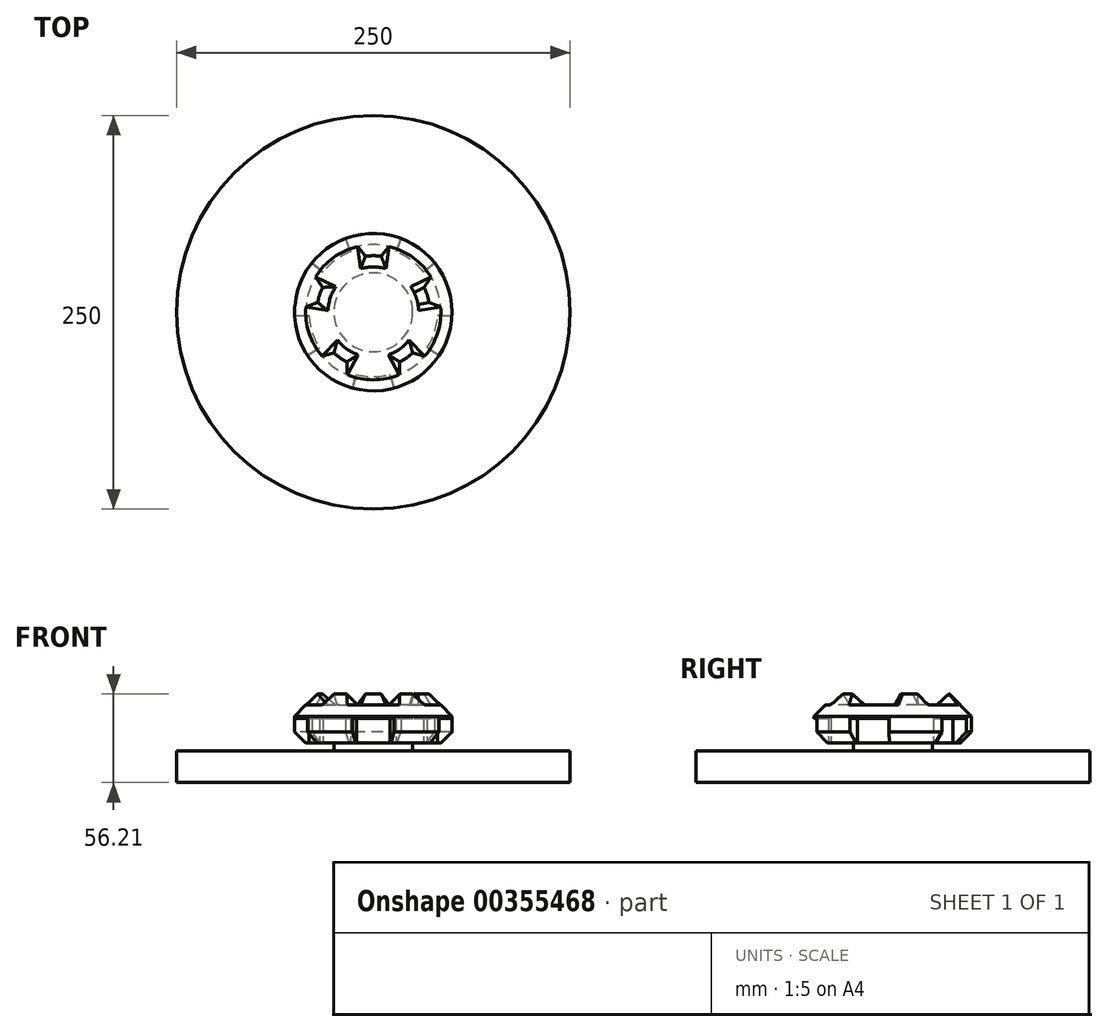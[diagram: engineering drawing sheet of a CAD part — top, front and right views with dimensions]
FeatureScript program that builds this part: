
annotation { "Feature Type Name" : "Feature", "Feature Type Description" : "" }
export const myFeature = defineFeature(function(context is Context, id is Id, definition is map)
    precondition{}
    {
        {
            var Q0;
            Q0=qCreatedBy(makeId("Top.planeOp"),FACE);
            var sketch = newSketch(context, id + "F0", { "sketchPlane" : qUnion([Q0])});
            skCircle(sketch, "E0", {"center": v(0, 0) * mm, "radius": 50 * mm});
            skSolve(sketch);
        }
        {
            var Q0;
            Q0=makeQuery(id+"F0.imprint","IMPRINT",FACE,{"disambiguationData":[TD([[makeQuery(id+"F0.imprint","IMPRINT",EDGE,{"derivedFrom":sQuery(id+"F0.wireOp",EDGE,"E0")}),1.0]])]});
            extrude(context, id + "F1", {"entities" : qUnion([Q0]), "depth" : 14.14 * mm, "hasSecondDirection" : true, "secondDirectionOppositeDirection" : true, "secondDirectionDepth" : 17.07 * mm});
        }
        {
            var Q0;
            Q0=makeQuery(id+"F1.opExtrude","CAP_EDGE",EDGE,{"disambiguationData":[OSD([sQuery(id+"F0.wireOp",EDGE,"E0")])],"isStart":false});
            chamfer(context, id + "F2", {"entities" : qUnion([Q0]), "width" : 14.14 * mm, "tangentPropagation" : true});
        }
        {
            var Q0;
            Q0=makeQuery(id+"F1.opExtrude","CAP_FACE",FACE,{"disambiguationData":[OSD([sQuery(id+"F0.wireOp",EDGE,"E0")])],"isStart":true});
            extrude(context, id + "F3", {"entities" : qUnion([Q0]), "oppositeDirection" : true, "depth" : 50 * mm});
        }
        {
            var Q0;
            Q0=makeQuery(id+"F3.opExtrude","CAP_EDGE",EDGE,{"disambiguationData":[OSD([sQuery(id+"F0.wireOp",EDGE,"E0")])],"isStart":true});
            chamfer(context, id + "F4", {"entities" : qUnion([Q0]), "chamferType" : ChamferType.OFFSET_ANGLE, "width" : 7.07 * mm, "oppositeDirection" : false, "angle" : 30 * degree, "tangentPropagation" : true});
        }
        {
            var Q0;
            Q0=makeQuery(id+"F1.opExtrude","CAP_EDGE",EDGE,{"disambiguationData":[OSD([sQuery(id+"F0.wireOp",EDGE,"E0")])],"isStart":true});
            chamfer(context, id + "F5", {"entities" : qUnion([Q0]), "width" : 7.07 * mm, "tangentPropagation" : true});
        }
        {
            var Q0;
            Q0=makeQuery(id+"F1.opExtrude","CAP_FACE",FACE,{"disambiguationData":[OSD([sQuery(id+"F0.wireOp",EDGE,"E0")])],"isStart":true});
            var sketch = newSketch(context, id + "F6", { "sketchPlane" : qUnion([Q0])});
            skCircle(sketch, "E1", {"center": v(0, 0) * mm, "radius": 25 * mm});
            skSolve(sketch);
        }
        {
            var Q0;
            Q0=makeQuery(id+"F6.imprint","IMPRINT",FACE,{"disambiguationData":[TD([[makeQuery(id+"F6.imprint","IMPRINT",EDGE,{"derivedFrom":sQuery(id+"F6.wireOp",EDGE,"E1")}),1.0]])]});
            extrude(context, id + "F7", {"entities" : qUnion([Q0]), "depth" : 5 * mm});
        }
        {
            var Q0;
            Q0=makeQuery(id+"F7.opExtrude","CAP_FACE",FACE,{"disambiguationData":[OSD([sQuery(id+"F6.wireOp",EDGE,"E1")])],"isStart":false});
            var sketch = newSketch(context, id + "F8", { "sketchPlane" : qUnion([Q0])});
            skCircle(sketch, "E2", {"center": v(0, 0) * mm, "radius": 125 * mm});
            skSolve(sketch);
        }
        {
            var Q0;
            Q0=makeQuery(id+"F8.imprint","IMPRINT",FACE,{"disambiguationData":[TD([[makeQuery(id+"F8.imprint","IMPRINT",EDGE,{"derivedFrom":makeQuery(id+"F7.opExtrude","CAP_EDGE",EDGE,{"disambiguationData":[OSD([sQuery(id+"F6.wireOp",EDGE,"E1")])],"isStart":false})}),1.0]])]});
            var Q1;
            Q1=makeQuery(id+"F8.imprint","IMPRINT",FACE,{"disambiguationData":[TD([[makeQuery(id+"F8.imprint","IMPRINT",EDGE,{"derivedFrom":sQuery(id+"F8.wireOp",EDGE,"E2")}),1.0]])]});
            extrude(context, id + "F9", {"entities" : qUnion([Q0, Q1]), "depth" : 20 * mm});
        }
        {
            var Q0;
            Q0=makeQuery(id+"F1.opExtrude","CAP_FACE",FACE,{"disambiguationData":[OSD([sQuery(id+"F0.wireOp",EDGE,"E0")])],"isStart":false});
            var sketch = newSketch(context, id + "F10", { "sketchPlane" : qUnion([Q0])});
            skCircle(sketch, "E3", {"center": v(0, 0) * mm, "radius": 35.86 * mm, "construction": true});
            skLineSegment(sketch, "E4.bottom", {"start": v(5, 35.5) * mm, "end": v(-5, 35.5) * mm, "construction": true});
            skLineSegment(sketch, "E4.top", {"start": v(5, 74.5) * mm, "end": v(-5, 74.5) * mm, "construction": true});
            skLineSegment(sketch, "E4.left", {"start": v(5, 35.5) * mm, "end": v(5, 74.5) * mm, "construction": true});
            skLineSegment(sketch, "E4.right", {"start": v(-5, 35.5) * mm, "end": v(-5, 74.5) * mm, "construction": true});
            skPoint(sketch, "E4.middle", {"position": v(0, 55) * mm});
            skLineSegment(sketch, "E5.bottom", {"start": v(32.22, 15.73) * mm, "end": v(69.3, 27.77) * mm, "construction": true});
            skLineSegment(sketch, "E5.top", {"start": v(35.31, 6.22) * mm, "end": v(72.4, 18.26) * mm, "construction": true});
            skLineSegment(sketch, "E5.left", {"start": v(32.22, 15.73) * mm, "end": v(35.31, 6.22) * mm, "construction": true});
            skLineSegment(sketch, "E5.right", {"start": v(69.3, 27.77) * mm, "end": v(72.4, 18.26) * mm, "construction": true});
            skPoint(sketch, "E5.middle", {"position": v(52.3, 17) * mm});
            skLineSegment(sketch, "E6.bottom", {"start": v(24.92, -25.79) * mm, "end": v(16.83, -31.67) * mm, "construction": true});
            skLineSegment(sketch, "E6.top", {"start": v(47.83, -57.33) * mm, "end": v(39.74, -63.2) * mm, "construction": true});
            skLineSegment(sketch, "E6.left", {"start": v(24.92, -25.79) * mm, "end": v(47.83, -57.33) * mm, "construction": true});
            skLineSegment(sketch, "E6.right", {"start": v(16.83, -31.67) * mm, "end": v(39.74, -63.2) * mm, "construction": true});
            skPoint(sketch, "E6.middle", {"position": v(32.33, -44.5) * mm});
            skLineSegment(sketch, "E7.bottom", {"start": v(-35.31, 6.22) * mm, "end": v(-72.4, 18.26) * mm, "construction": true});
            skLineSegment(sketch, "E7.top", {"start": v(-32.22, 15.73) * mm, "end": v(-69.3, 27.77) * mm, "construction": true});
            skLineSegment(sketch, "E7.left", {"start": v(-35.31, 6.22) * mm, "end": v(-32.22, 15.73) * mm, "construction": true});
            skLineSegment(sketch, "E7.right", {"start": v(-72.4, 18.26) * mm, "end": v(-69.3, 27.77) * mm, "construction": true});
            skPoint(sketch, "E7.middle", {"position": v(-52.3, 17) * mm});
            skLineSegment(sketch, "E8.bottom", {"start": v(-16.83, -31.67) * mm, "end": v(-24.92, -25.79) * mm, "construction": true});
            skLineSegment(sketch, "E8.top", {"start": v(-39.74, -63.2) * mm, "end": v(-47.83, -57.33) * mm, "construction": true});
            skLineSegment(sketch, "E8.left", {"start": v(-16.83, -31.67) * mm, "end": v(-39.74, -63.2) * mm, "construction": true});
            skLineSegment(sketch, "E8.right", {"start": v(-24.92, -25.79) * mm, "end": v(-47.83, -57.33) * mm, "construction": true});
            skPoint(sketch, "E8.middle", {"position": v(-32.33, -44.5) * mm});
            skCircle(sketch, "E9", {"center": v(0, 0) * mm, "radius": 50 * mm, "construction": true});
            skLineSegment(sketch, "E10", {"start": v(6.97, 49.51) * mm, "end": v(0, 0) * mm, "construction": true});
            skLineSegment(sketch, "E11", {"start": v(44.93, 21.93) * mm, "end": v(0, 0) * mm, "construction": true});
            skLineSegment(sketch, "E12", {"start": v(0, 0) * mm, "end": v(49.24, 8.67) * mm, "construction": true});
            skLineSegment(sketch, "E13", {"start": v(34.74, -35.96) * mm, "end": v(0, 0) * mm, "construction": true});
            skLineSegment(sketch, "E14", {"start": v(23.46, -44.15) * mm, "end": v(0, 0) * mm, "construction": true});
            skLineSegment(sketch, "E15", {"start": v(-23.46, -44.15) * mm, "end": v(0, 0) * mm, "construction": true});
            skLineSegment(sketch, "E16", {"start": v(-34.74, -35.96) * mm, "end": v(0, 0) * mm, "construction": true});
            skLineSegment(sketch, "E17", {"start": v(-49.24, 8.67) * mm, "end": v(0, 0) * mm, "construction": true});
            skLineSegment(sketch, "E18", {"start": v(-44.93, 21.93) * mm, "end": v(0, 0) * mm, "construction": true});
            skLineSegment(sketch, "E19", {"start": v(-6.97, 49.51) * mm, "end": v(0, 0) * mm, "construction": true});
            skArc(sketch, "E20", {"start": v(6.97, 49.51) * mm, "mid": v(29.39, 40.45) * mm, "end": v(44.93, 21.93) * mm});
            skArc(sketch, "E21", {"start": v(49.24, 8.67) * mm, "mid": v(47.55, -15.45) * mm, "end": v(34.74, -35.96) * mm});
            skArc(sketch, "E22", {"start": v(23.46, -44.15) * mm, "mid": v(0, -50) * mm, "end": v(-23.46, -44.15) * mm});
            skArc(sketch, "E23", {"start": v(-34.74, -35.96) * mm, "mid": v(-47.55, -15.45) * mm, "end": v(-49.24, 8.67) * mm});
            skArc(sketch, "E24", {"start": v(-44.93, 21.93) * mm, "mid": v(-29.39, 40.45) * mm, "end": v(-6.97, 49.51) * mm});
            skCircle(sketch, "E25", {"center": v(0, 0) * mm, "radius": 28.79 * mm, "construction": true});
            skLineSegment(sketch, "E26", {"start": v(-6.97, 49.51) * mm, "end": v(-4.01, 28.5) * mm});
            skLineSegment(sketch, "E27", {"start": v(4.01, 28.5) * mm, "end": v(6.97, 49.51) * mm});
            skLineSegment(sketch, "E28", {"start": v(25.87, 12.63) * mm, "end": v(44.93, 21.93) * mm});
            skLineSegment(sketch, "E29", {"start": v(28.35, 5) * mm, "end": v(49.24, 8.67) * mm});
            skLineSegment(sketch, "E30", {"start": v(20, -20.7) * mm, "end": v(34.74, -35.96) * mm});
            skLineSegment(sketch, "E31", {"start": v(13.5, -25.42) * mm, "end": v(23.46, -44.15) * mm});
            skLineSegment(sketch, "E32", {"start": v(-13.5, -25.42) * mm, "end": v(-23.46, -44.15) * mm});
            skLineSegment(sketch, "E33", {"start": v(-20, -20.7) * mm, "end": v(-34.74, -35.96) * mm});
            skLineSegment(sketch, "E34", {"start": v(-28.35, 5) * mm, "end": v(-49.24, 8.67) * mm});
            skLineSegment(sketch, "E35", {"start": v(-25.87, 12.63) * mm, "end": v(-44.93, 21.93) * mm});
            skArc(sketch, "E36", {"start": v(-4.01, 28.5) * mm, "mid": v(0, 28.79) * mm, "end": v(4.01, 28.5) * mm});
            skArc(sketch, "E37", {"start": v(25.87, 12.63) * mm, "mid": v(27.38, 8.9) * mm, "end": v(28.35, 5) * mm});
            skArc(sketch, "E38", {"start": v(20, -20.7) * mm, "mid": v(16.92, -23.29) * mm, "end": v(13.5, -25.42) * mm});
            skArc(sketch, "E39", {"start": v(-13.5, -25.42) * mm, "mid": v(-16.92, -23.29) * mm, "end": v(-20, -20.7) * mm});
            skArc(sketch, "E40", {"start": v(-28.35, 5) * mm, "mid": v(-27.38, 8.9) * mm, "end": v(-25.87, 12.63) * mm});
            skCircle(sketch, "E41.cCircle", {"center": v(0, 0) * mm, "radius": 55 * mm, "construction": true});
            skLineSegment(sketch, "E41.0", {"start": v(32.33, 44.5) * mm, "end": v(52.3, 17) * mm, "construction": true});
            skLineSegment(sketch, "E41.1", {"start": v(52.3, 17) * mm, "end": v(52.3, -17) * mm, "construction": true});
            skLineSegment(sketch, "E41.2", {"start": v(52.3, -17) * mm, "end": v(32.33, -44.5) * mm, "construction": true});
            skLineSegment(sketch, "E41.3", {"start": v(32.33, -44.5) * mm, "end": v(0, -55) * mm, "construction": true});
            skLineSegment(sketch, "E41.4", {"start": v(0, -55) * mm, "end": v(-32.33, -44.5) * mm, "construction": true});
            skLineSegment(sketch, "E41.5", {"start": v(-32.33, -44.5) * mm, "end": v(-52.3, -17) * mm, "construction": true});
            skLineSegment(sketch, "E41.6", {"start": v(-52.3, -17) * mm, "end": v(-52.3, 17) * mm, "construction": true});
            skLineSegment(sketch, "E41.7", {"start": v(-52.3, 17) * mm, "end": v(-32.33, 44.5) * mm, "construction": true});
            skLineSegment(sketch, "E41.8", {"start": v(-32.33, 44.5) * mm, "end": v(0, 55) * mm, "construction": true});
            skLineSegment(sketch, "E41.9", {"start": v(0, 55) * mm, "end": v(32.33, 44.5) * mm, "construction": true});
            skSolve(sketch);
        }
        {
            var Q0;
            Q0 = qSketchRegion(id + "F10", true);
            extrude(context, id + "F11", {"entities" : qUnion([Q0]), "operationType" : NewBodyOperationType.REMOVE, "oppositeDirection" : true, "depth" : 7.07 * mm});
        }
        {
            var Q0;
            Q0=makeQuery(id+"F11.boolean.opBoolean","COPY",EDGE,{"derivedFrom":makeQuery(id+"F11.opExtrude","CAP_EDGE",EDGE,{"disambiguationData":[OSD([sQuery(id+"F10.wireOp",EDGE,"E40")])],"isStart":true})});
            var Q1;
            Q1=makeQuery(id+"F11.boolean.opBoolean","COPY",EDGE,{"derivedFrom":makeQuery(id+"F11.opExtrude","CAP_EDGE",EDGE,{"disambiguationData":[OSD([sQuery(id+"F10.wireOp",EDGE,"E36")])],"isStart":true})});
            var Q2;
            Q2=makeQuery(id+"F11.boolean.opBoolean","COPY",EDGE,{"derivedFrom":makeQuery(id+"F11.opExtrude","CAP_EDGE",EDGE,{"disambiguationData":[OSD([sQuery(id+"F10.wireOp",EDGE,"E37")])],"isStart":true})});
            var Q3;
            Q3=makeQuery(id+"F11.boolean.opBoolean","COPY",EDGE,{"derivedFrom":makeQuery(id+"F11.opExtrude","CAP_EDGE",EDGE,{"disambiguationData":[OSD([sQuery(id+"F10.wireOp",EDGE,"E38")])],"isStart":true})});
            var Q4;
            Q4=makeQuery(id+"F11.boolean.opBoolean","COPY",EDGE,{"derivedFrom":makeQuery(id+"F11.opExtrude","CAP_EDGE",EDGE,{"disambiguationData":[OSD([sQuery(id+"F10.wireOp",EDGE,"E39")])],"isStart":true})});
            chamfer(context, id + "F12", {"entities" : qUnion([Q0, Q1, Q2, Q3, Q4]), "width" : 7.07 * mm, "tangentPropagation" : true});
        }
        {
            var Q0;
            Q0=makeQuery(id+"F11.boolean.opBoolean","COPY",EDGE,{"derivedFrom":makeQuery(id+"F11.opExtrude","CAP_EDGE",EDGE,{"disambiguationData":[OSD([sQuery(id+"F10.wireOp",EDGE,"E34")])],"isStart":false})});
            var Q1;
            Q1=makeQuery(id+"F11.boolean.opBoolean","COPY",EDGE,{"derivedFrom":makeQuery(id+"F11.opExtrude","CAP_EDGE",EDGE,{"disambiguationData":[OSD([sQuery(id+"F10.wireOp",EDGE,"E33")])],"isStart":false})});
            var Q2;
            Q2=makeQuery(id+"F11.boolean.opBoolean","COPY",EDGE,{"derivedFrom":makeQuery(id+"F11.opExtrude","CAP_EDGE",EDGE,{"disambiguationData":[OSD([sQuery(id+"F10.wireOp",EDGE,"E32")])],"isStart":false})});
            var Q3;
            Q3=makeQuery(id+"F11.boolean.opBoolean","COPY",EDGE,{"derivedFrom":makeQuery(id+"F11.opExtrude","CAP_EDGE",EDGE,{"disambiguationData":[OSD([sQuery(id+"F10.wireOp",EDGE,"E31")])],"isStart":false})});
            var Q4;
            Q4=makeQuery(id+"F11.boolean.opBoolean","COPY",EDGE,{"derivedFrom":makeQuery(id+"F11.opExtrude","CAP_EDGE",EDGE,{"disambiguationData":[OSD([sQuery(id+"F10.wireOp",EDGE,"E30")])],"isStart":false})});
            var Q5;
            Q5=makeQuery(id+"F11.boolean.opBoolean","COPY",EDGE,{"derivedFrom":makeQuery(id+"F11.opExtrude","CAP_EDGE",EDGE,{"disambiguationData":[OSD([sQuery(id+"F10.wireOp",EDGE,"E29")])],"isStart":false})});
            var Q6;
            Q6=makeQuery(id+"F11.boolean.opBoolean","COPY",EDGE,{"derivedFrom":makeQuery(id+"F11.opExtrude","CAP_EDGE",EDGE,{"disambiguationData":[OSD([sQuery(id+"F10.wireOp",EDGE,"E28")])],"isStart":false})});
            var Q7;
            Q7=makeQuery(id+"F11.boolean.opBoolean","COPY",EDGE,{"derivedFrom":makeQuery(id+"F11.opExtrude","CAP_EDGE",EDGE,{"disambiguationData":[OSD([sQuery(id+"F10.wireOp",EDGE,"E27")])],"isStart":false})});
            var Q8;
            Q8=makeQuery(id+"F11.boolean.opBoolean","COPY",EDGE,{"derivedFrom":makeQuery(id+"F11.opExtrude","CAP_EDGE",EDGE,{"disambiguationData":[OSD([sQuery(id+"F10.wireOp",EDGE,"E26")])],"isStart":false})});
            var Q9;
            Q9=makeQuery(id+"F11.boolean.opBoolean","COPY",EDGE,{"derivedFrom":makeQuery(id+"F11.opExtrude","CAP_EDGE",EDGE,{"disambiguationData":[OSD([sQuery(id+"F10.wireOp",EDGE,"E35")])],"isStart":false})});
            chamfer(context, id + "F13", {"entities" : qUnion([Q0, Q1, Q2, Q3, Q4, Q5, Q6, Q7, Q8, Q9]), "chamferType" : ChamferType.OFFSET_ANGLE, "width" : 7.07 * mm, "oppositeDirection" : true, "angle" : 30 * degree, "tangentPropagation" : true});
        }
        {
            var Q0;
            Q0=makeQuery(id+"F1.opExtrude","CAP_FACE",FACE,{"disambiguationData":[OSD([sQuery(id+"F0.wireOp",EDGE,"E0")])],"isStart":true});
            var sketch = newSketch(context, id + "F14", { "sketchPlane" : qUnion([Q0])});
            skCircle(sketch, "E42", {"center": v(0, 0) * mm, "radius": 47.5 * mm, "construction": true});
            skCircle(sketch, "E43", {"center": v(0, 0) * mm, "radius": 50 * mm, "construction": true});
            skCircle(sketch, "E44.cCircle", {"center": v(0, 0) * mm, "radius": 55 * mm});
            skLineSegment(sketch, "E44.0", {"start": v(32.33, 44.5) * mm, "end": v(52.3, 17) * mm, "construction": true});
            skLineSegment(sketch, "E44.1", {"start": v(52.3, 17) * mm, "end": v(52.3, -17) * mm, "construction": true});
            skLineSegment(sketch, "E44.2", {"start": v(52.3, -17) * mm, "end": v(32.33, -44.5) * mm, "construction": true});
            skLineSegment(sketch, "E44.3", {"start": v(32.33, -44.5) * mm, "end": v(0, -55) * mm, "construction": true});
            skLineSegment(sketch, "E44.4", {"start": v(0, -55) * mm, "end": v(-32.33, -44.5) * mm, "construction": true});
            skLineSegment(sketch, "E44.5", {"start": v(-32.33, -44.5) * mm, "end": v(-52.3, -17) * mm, "construction": true});
            skLineSegment(sketch, "E44.6", {"start": v(-52.3, -17) * mm, "end": v(-52.3, 17) * mm, "construction": true});
            skLineSegment(sketch, "E44.7", {"start": v(-52.3, 17) * mm, "end": v(-32.33, 44.5) * mm, "construction": true});
            skLineSegment(sketch, "E44.8", {"start": v(-32.33, 44.5) * mm, "end": v(0, 55) * mm, "construction": true});
            skLineSegment(sketch, "E44.9", {"start": v(0, 55) * mm, "end": v(32.33, 44.5) * mm, "construction": true});
            skCircle(sketch, "E45", {"center": v(0, 0) * mm, "radius": 40.92 * mm, "construction": true});
            skLineSegment(sketch, "E46.bottom", {"start": v(12.5, 45.83) * mm, "end": v(-12.5, 45.83) * mm, "construction": true});
            skLineSegment(sketch, "E46.top", {"start": v(12.5, 64.17) * mm, "end": v(-12.5, 64.17) * mm, "construction": true});
            skLineSegment(sketch, "E46.left", {"start": v(12.5, 45.83) * mm, "end": v(12.5, 64.17) * mm, "construction": true});
            skLineSegment(sketch, "E46.right", {"start": v(-12.5, 45.83) * mm, "end": v(-12.5, 64.17) * mm, "construction": true});
            skPoint(sketch, "E46.middle", {"position": v(0, 55) * mm});
            skLineSegment(sketch, "E47.bottom", {"start": v(47.45, 2.27) * mm, "end": v(64.9, 7.94) * mm, "construction": true});
            skLineSegment(sketch, "E47.top", {"start": v(39.72, 26.05) * mm, "end": v(57.17, 31.72) * mm, "construction": true});
            skLineSegment(sketch, "E47.left", {"start": v(47.45, 2.27) * mm, "end": v(39.72, 26.05) * mm, "construction": true});
            skLineSegment(sketch, "E47.right", {"start": v(64.9, 7.94) * mm, "end": v(57.17, 31.72) * mm, "construction": true});
            skPoint(sketch, "E47.middle", {"position": v(52.3, 17) * mm});
            skLineSegment(sketch, "E48.bottom", {"start": v(16.82, -44.42) * mm, "end": v(37.05, -29.73) * mm, "construction": true});
            skLineSegment(sketch, "E48.top", {"start": v(27.6, -59.27) * mm, "end": v(47.83, -44.57) * mm, "construction": true});
            skLineSegment(sketch, "E48.left", {"start": v(16.82, -44.42) * mm, "end": v(27.6, -59.27) * mm, "construction": true});
            skLineSegment(sketch, "E48.right", {"start": v(37.05, -29.73) * mm, "end": v(47.83, -44.57) * mm, "construction": true});
            skPoint(sketch, "E48.middle", {"position": v(32.33, -44.5) * mm});
            skLineSegment(sketch, "E49.bottom", {"start": v(-16.82, -44.42) * mm, "end": v(-37.05, -29.73) * mm, "construction": true});
            skLineSegment(sketch, "E49.top", {"start": v(-27.6, -59.27) * mm, "end": v(-47.83, -44.57) * mm, "construction": true});
            skLineSegment(sketch, "E49.left", {"start": v(-16.82, -44.42) * mm, "end": v(-27.6, -59.27) * mm, "construction": true});
            skLineSegment(sketch, "E49.right", {"start": v(-37.05, -29.73) * mm, "end": v(-47.83, -44.57) * mm, "construction": true});
            skPoint(sketch, "E49.middle", {"position": v(-32.33, -44.5) * mm});
            skLineSegment(sketch, "E50.bottom", {"start": v(-47.45, 2.27) * mm, "end": v(-64.9, 7.94) * mm, "construction": true});
            skLineSegment(sketch, "E50.top", {"start": v(-39.72, 26.05) * mm, "end": v(-57.17, 31.72) * mm, "construction": true});
            skLineSegment(sketch, "E50.left", {"start": v(-47.45, 2.27) * mm, "end": v(-39.72, 26.05) * mm, "construction": true});
            skLineSegment(sketch, "E50.right", {"start": v(-64.9, 7.94) * mm, "end": v(-57.17, 31.72) * mm, "construction": true});
            skPoint(sketch, "E50.middle", {"position": v(-52.3, 17) * mm});
            skLineSegment(sketch, "E51", {"start": v(13.16, 48.24) * mm, "end": v(0, 0) * mm, "construction": true});
            skLineSegment(sketch, "E52", {"start": v(41.81, 27.42) * mm, "end": v(0, 0) * mm, "construction": true});
            skLineSegment(sketch, "E53", {"start": v(49.94, 2.4) * mm, "end": v(0, 0) * mm, "construction": true});
            skLineSegment(sketch, "E54", {"start": v(39, -31.3) * mm, "end": v(0, 0) * mm, "construction": true});
            skLineSegment(sketch, "E55", {"start": v(17.7, -46.76) * mm, "end": v(0, 0) * mm, "construction": true});
            skLineSegment(sketch, "E56", {"start": v(-17.7, -46.76) * mm, "end": v(0, 0) * mm, "construction": true});
            skLineSegment(sketch, "E57", {"start": v(-39, -31.3) * mm, "end": v(0, 0) * mm, "construction": true});
            skLineSegment(sketch, "E58", {"start": v(-49.94, 2.4) * mm, "end": v(0, 0) * mm, "construction": true});
            skLineSegment(sketch, "E59", {"start": v(-41.81, 27.42) * mm, "end": v(0, 0) * mm, "construction": true});
            skLineSegment(sketch, "E60", {"start": v(-13.16, 48.24) * mm, "end": v(0, 0) * mm, "construction": true});
            skArc(sketch, "E61", {"start": v(13.16, 48.24) * mm, "mid": v(29.39, 40.45) * mm, "end": v(41.81, 27.42) * mm});
            skArc(sketch, "E62", {"start": v(49.94, 2.4) * mm, "mid": v(47.55, -15.45) * mm, "end": v(39, -31.3) * mm});
            skArc(sketch, "E63", {"start": v(17.7, -46.76) * mm, "mid": v(0, -50) * mm, "end": v(-17.7, -46.76) * mm});
            skArc(sketch, "E64", {"start": v(-39, -31.3) * mm, "mid": v(-47.55, -15.45) * mm, "end": v(-49.94, 2.4) * mm});
            skArc(sketch, "E65", {"start": v(-41.81, 27.42) * mm, "mid": v(-29.39, 40.45) * mm, "end": v(-13.16, 48.24) * mm});
            skArc(sketch, "E66", {"start": v(-10.77, 39.48) * mm, "mid": v(0, 40.92) * mm, "end": v(10.77, 39.48) * mm});
            skArc(sketch, "E67", {"start": v(34.22, 22.44) * mm, "mid": v(38.91, 12.64) * mm, "end": v(40.87, 1.96) * mm});
            skArc(sketch, "E68", {"start": v(31.91, -25.6) * mm, "mid": v(24.05, -33.1) * mm, "end": v(14.5, -38.27) * mm});
            skArc(sketch, "E69", {"start": v(-14.5, -38.27) * mm, "mid": v(-24.05, -33.1) * mm, "end": v(-31.91, -25.6) * mm});
            skArc(sketch, "E70", {"start": v(-40.87, 1.96) * mm, "mid": v(-38.91, 12.64) * mm, "end": v(-34.22, 22.44) * mm});
            skLineSegment(sketch, "E71", {"start": v(-41.81, 27.42) * mm, "end": v(-34.22, 22.44) * mm});
            skLineSegment(sketch, "E72", {"start": v(-49.94, 2.4) * mm, "end": v(-40.87, 1.96) * mm});
            skLineSegment(sketch, "E73", {"start": v(-13.16, 48.24) * mm, "end": v(-10.77, 39.48) * mm});
            skLineSegment(sketch, "E74", {"start": v(13.16, 48.24) * mm, "end": v(10.77, 39.48) * mm});
            skLineSegment(sketch, "E75", {"start": v(41.81, 27.42) * mm, "end": v(34.22, 22.44) * mm});
            skLineSegment(sketch, "E76", {"start": v(49.94, 2.4) * mm, "end": v(40.87, 1.96) * mm});
            skLineSegment(sketch, "E77", {"start": v(39, -31.3) * mm, "end": v(31.91, -25.6) * mm});
            skLineSegment(sketch, "E78", {"start": v(17.7, -46.76) * mm, "end": v(14.5, -38.27) * mm});
            skLineSegment(sketch, "E79", {"start": v(-17.7, -46.76) * mm, "end": v(-14.5, -38.27) * mm});
            skLineSegment(sketch, "E80", {"start": v(-39, -31.3) * mm, "end": v(-31.91, -25.6) * mm});
            skSolve(sketch);
        }
        {
            var Q0;
            Q0 = qSketchRegion(id + "F14", true);
            var Q1;
            Q1 = qConstructionFilter(qBodyType(qCreatedBy(id + "F14" ,EDGE), BodyType.WIRE), ConstructionObject.NO);
            extrude(context, id + "F15", {"entities" : qUnion([Q0]), "operationType" : NewBodyOperationType.REMOVE, "surfaceEntities" : qUnion([Q1]), "oppositeDirection" : true, "depth" : 15.73 * mm});
        }
        {
            var Q0;
            Q0=makeQuery(id+"F15.boolean.opBoolean","COPY",EDGE,{"disambiguationData":[OD(0.0)],"derivedFrom":makeQuery(id+"F15.opExtrude","CAP_EDGE",EDGE,{"disambiguationData":[OSD([sQuery(id+"F14.wireOp",EDGE,"E70")])],"isStart":false})});
            var Q1;
            Q1=makeQuery(id+"F15.boolean.opBoolean","COPY",EDGE,{"disambiguationData":[OD(0.0)],"derivedFrom":makeQuery(id+"F15.opExtrude","CAP_EDGE",EDGE,{"disambiguationData":[OSD([sQuery(id+"F14.wireOp",EDGE,"E69")])],"isStart":false})});
            var Q2;
            Q2=makeQuery(id+"F15.boolean.opBoolean","COPY",EDGE,{"disambiguationData":[OD(0.0)],"derivedFrom":makeQuery(id+"F15.opExtrude","CAP_EDGE",EDGE,{"disambiguationData":[OSD([sQuery(id+"F14.wireOp",EDGE,"E68")])],"isStart":false})});
            var Q3;
            Q3=makeQuery(id+"F15.boolean.opBoolean","COPY",EDGE,{"disambiguationData":[OD(0.0)],"derivedFrom":makeQuery(id+"F15.opExtrude","CAP_EDGE",EDGE,{"disambiguationData":[OSD([sQuery(id+"F14.wireOp",EDGE,"E67")])],"isStart":false})});
            var Q4;
            Q4=makeQuery(id+"F15.boolean.opBoolean","COPY",EDGE,{"disambiguationData":[OD(0.0)],"derivedFrom":makeQuery(id+"F15.opExtrude","CAP_EDGE",EDGE,{"disambiguationData":[OSD([sQuery(id+"F14.wireOp",EDGE,"E66")])],"isStart":false})});
            chamfer(context, id + "F16", {"entities" : qUnion([Q0, Q1, Q2, Q3, Q4]), "chamferType" : ChamferType.OFFSET_ANGLE, "width" : 15.73 * mm, "oppositeDirection" : true, "angle" : 30 * degree, "tangentPropagation" : true});
        }
        {
            var Q0;
            Q0=makeQuery(id+"F16.opChamfer","BLEND_EDGE",EDGE,{"blendedFrom":[makeQuery(id+"F15.boolean.opBoolean","COPY",EDGE,{"derivedFrom":makeQuery(id+"F15.opExtrude","CAP_EDGE",EDGE,{"disambiguationData":[OSD([sQuery(id+"F14.wireOp",EDGE,"E66")])],"isStart":false})}),makeQuery(id+"F15.boolean.opBoolean","COPY",FACE,{"derivedFrom":makeQuery(id+"F15.opExtrude","SWEPT_FACE",FACE,{"disambiguationData":[OSD([sQuery(id+"F14.wireOp",EDGE,"E73")])]})})],"blendedInto":[makeQuery(id+"F15.boolean.opBoolean","COPY",FACE,{"derivedFrom":makeQuery(id+"F15.opExtrude","SWEPT_FACE",FACE,{"disambiguationData":[OSD([sQuery(id+"F14.wireOp",EDGE,"E73")])]})})]});
            var Q1;
            Q1=makeQuery(id+"F16.opChamfer","BLEND_EDGE",EDGE,{"blendedFrom":[makeQuery(id+"F15.boolean.opBoolean","COPY",EDGE,{"derivedFrom":makeQuery(id+"F15.opExtrude","CAP_EDGE",EDGE,{"disambiguationData":[OSD([sQuery(id+"F14.wireOp",EDGE,"E66")])],"isStart":false})}),makeQuery(id+"F15.boolean.opBoolean","COPY",FACE,{"derivedFrom":makeQuery(id+"F15.opExtrude","SWEPT_FACE",FACE,{"disambiguationData":[OSD([sQuery(id+"F14.wireOp",EDGE,"E74")])]})})],"blendedInto":[makeQuery(id+"F15.boolean.opBoolean","COPY",FACE,{"derivedFrom":makeQuery(id+"F15.opExtrude","SWEPT_FACE",FACE,{"disambiguationData":[OSD([sQuery(id+"F14.wireOp",EDGE,"E74")])]})})]});
            var Q2;
            Q2=makeQuery(id+"F16.opChamfer","BLEND_EDGE",EDGE,{"blendedFrom":[makeQuery(id+"F15.boolean.opBoolean","COPY",EDGE,{"derivedFrom":makeQuery(id+"F15.opExtrude","CAP_EDGE",EDGE,{"disambiguationData":[OSD([sQuery(id+"F14.wireOp",EDGE,"E67")])],"isStart":false})}),makeQuery(id+"F15.boolean.opBoolean","COPY",FACE,{"derivedFrom":makeQuery(id+"F15.opExtrude","SWEPT_FACE",FACE,{"disambiguationData":[OSD([sQuery(id+"F14.wireOp",EDGE,"E75")])]})})],"blendedInto":[makeQuery(id+"F15.boolean.opBoolean","COPY",FACE,{"derivedFrom":makeQuery(id+"F15.opExtrude","SWEPT_FACE",FACE,{"disambiguationData":[OSD([sQuery(id+"F14.wireOp",EDGE,"E75")])]})})]});
            var Q3;
            Q3=makeQuery(id+"F16.opChamfer","BLEND_EDGE",EDGE,{"blendedFrom":[makeQuery(id+"F15.boolean.opBoolean","COPY",EDGE,{"derivedFrom":makeQuery(id+"F15.opExtrude","CAP_EDGE",EDGE,{"disambiguationData":[OSD([sQuery(id+"F14.wireOp",EDGE,"E67")])],"isStart":false})}),makeQuery(id+"F15.boolean.opBoolean","COPY",FACE,{"derivedFrom":makeQuery(id+"F15.opExtrude","SWEPT_FACE",FACE,{"disambiguationData":[OSD([sQuery(id+"F14.wireOp",EDGE,"E76")])]})})],"blendedInto":[makeQuery(id+"F15.boolean.opBoolean","COPY",FACE,{"derivedFrom":makeQuery(id+"F15.opExtrude","SWEPT_FACE",FACE,{"disambiguationData":[OSD([sQuery(id+"F14.wireOp",EDGE,"E76")])]})})]});
            var Q4;
            Q4=makeQuery(id+"F16.opChamfer","BLEND_EDGE",EDGE,{"blendedFrom":[makeQuery(id+"F15.boolean.opBoolean","COPY",EDGE,{"derivedFrom":makeQuery(id+"F15.opExtrude","CAP_EDGE",EDGE,{"disambiguationData":[OSD([sQuery(id+"F14.wireOp",EDGE,"E68")])],"isStart":false})}),makeQuery(id+"F15.boolean.opBoolean","COPY",FACE,{"derivedFrom":makeQuery(id+"F15.opExtrude","SWEPT_FACE",FACE,{"disambiguationData":[OSD([sQuery(id+"F14.wireOp",EDGE,"E77")])]})})],"blendedInto":[makeQuery(id+"F15.boolean.opBoolean","COPY",FACE,{"derivedFrom":makeQuery(id+"F15.opExtrude","SWEPT_FACE",FACE,{"disambiguationData":[OSD([sQuery(id+"F14.wireOp",EDGE,"E77")])]})})]});
            var Q5;
            Q5=makeQuery(id+"F16.opChamfer","BLEND_EDGE",EDGE,{"blendedFrom":[makeQuery(id+"F15.boolean.opBoolean","COPY",EDGE,{"derivedFrom":makeQuery(id+"F15.opExtrude","CAP_EDGE",EDGE,{"disambiguationData":[OSD([sQuery(id+"F14.wireOp",EDGE,"E68")])],"isStart":false})}),makeQuery(id+"F15.boolean.opBoolean","COPY",FACE,{"derivedFrom":makeQuery(id+"F15.opExtrude","SWEPT_FACE",FACE,{"disambiguationData":[OSD([sQuery(id+"F14.wireOp",EDGE,"E78")])]})})],"blendedInto":[makeQuery(id+"F15.boolean.opBoolean","COPY",FACE,{"derivedFrom":makeQuery(id+"F15.opExtrude","SWEPT_FACE",FACE,{"disambiguationData":[OSD([sQuery(id+"F14.wireOp",EDGE,"E78")])]})})]});
            var Q6;
            Q6=makeQuery(id+"F16.opChamfer","BLEND_EDGE",EDGE,{"blendedFrom":[makeQuery(id+"F15.boolean.opBoolean","COPY",EDGE,{"derivedFrom":makeQuery(id+"F15.opExtrude","CAP_EDGE",EDGE,{"disambiguationData":[OSD([sQuery(id+"F14.wireOp",EDGE,"E69")])],"isStart":false})}),makeQuery(id+"F15.boolean.opBoolean","COPY",FACE,{"derivedFrom":makeQuery(id+"F15.opExtrude","SWEPT_FACE",FACE,{"disambiguationData":[OSD([sQuery(id+"F14.wireOp",EDGE,"E79")])]})})],"blendedInto":[makeQuery(id+"F15.boolean.opBoolean","COPY",FACE,{"derivedFrom":makeQuery(id+"F15.opExtrude","SWEPT_FACE",FACE,{"disambiguationData":[OSD([sQuery(id+"F14.wireOp",EDGE,"E79")])]})})]});
            var Q7;
            Q7=makeQuery(id+"F16.opChamfer","BLEND_EDGE",EDGE,{"blendedFrom":[makeQuery(id+"F15.boolean.opBoolean","COPY",EDGE,{"derivedFrom":makeQuery(id+"F15.opExtrude","CAP_EDGE",EDGE,{"disambiguationData":[OSD([sQuery(id+"F14.wireOp",EDGE,"E69")])],"isStart":false})}),makeQuery(id+"F15.boolean.opBoolean","COPY",FACE,{"derivedFrom":makeQuery(id+"F15.opExtrude","SWEPT_FACE",FACE,{"disambiguationData":[OSD([sQuery(id+"F14.wireOp",EDGE,"E80")])]})})],"blendedInto":[makeQuery(id+"F15.boolean.opBoolean","COPY",FACE,{"derivedFrom":makeQuery(id+"F15.opExtrude","SWEPT_FACE",FACE,{"disambiguationData":[OSD([sQuery(id+"F14.wireOp",EDGE,"E80")])]})})]});
            var Q8;
            Q8=makeQuery(id+"F16.opChamfer","BLEND_EDGE",EDGE,{"blendedFrom":[makeQuery(id+"F15.boolean.opBoolean","COPY",EDGE,{"derivedFrom":makeQuery(id+"F15.opExtrude","CAP_EDGE",EDGE,{"disambiguationData":[OSD([sQuery(id+"F14.wireOp",EDGE,"E70")])],"isStart":false})}),makeQuery(id+"F15.boolean.opBoolean","COPY",FACE,{"derivedFrom":makeQuery(id+"F15.opExtrude","SWEPT_FACE",FACE,{"disambiguationData":[OSD([sQuery(id+"F14.wireOp",EDGE,"E72")])]})})],"blendedInto":[makeQuery(id+"F15.boolean.opBoolean","COPY",FACE,{"derivedFrom":makeQuery(id+"F15.opExtrude","SWEPT_FACE",FACE,{"disambiguationData":[OSD([sQuery(id+"F14.wireOp",EDGE,"E72")])]})})]});
            var Q9;
            Q9=makeQuery(id+"F16.opChamfer","BLEND_EDGE",EDGE,{"blendedFrom":[makeQuery(id+"F15.boolean.opBoolean","COPY",EDGE,{"derivedFrom":makeQuery(id+"F15.opExtrude","CAP_EDGE",EDGE,{"disambiguationData":[OSD([sQuery(id+"F14.wireOp",EDGE,"E70")])],"isStart":false})}),makeQuery(id+"F15.boolean.opBoolean","COPY",FACE,{"derivedFrom":makeQuery(id+"F15.opExtrude","SWEPT_FACE",FACE,{"disambiguationData":[OSD([sQuery(id+"F14.wireOp",EDGE,"E71")])]})})],"blendedInto":[makeQuery(id+"F15.boolean.opBoolean","COPY",FACE,{"derivedFrom":makeQuery(id+"F15.opExtrude","SWEPT_FACE",FACE,{"disambiguationData":[OSD([sQuery(id+"F14.wireOp",EDGE,"E71")])]})})]});
            chamfer(context, id + "F17", {"entities" : qUnion([Q0, Q1, Q2, Q3, Q4, Q5, Q6, Q7, Q8, Q9]), "chamferType" : ChamferType.OFFSET_ANGLE, "width" : 5 * mm, "oppositeDirection" : false, "angle" : 60 * degree, "tangentPropagation" : true});
        }
        {
            var Q0;
            Q0=makeQuery(id+"F1.opExtrude","SWEPT_BODY",BODY,{"disambiguationData":[OSD([sQuery(id+"F0.wireOp",EDGE,"E0")])]});
            var Q1;
            Q1=makeQuery(id+"F3.opExtrude","SWEPT_BODY",BODY,{"disambiguationData":[OSD([sQuery(id+"F0.wireOp",EDGE,"E0")])]});
            booleanBodies(context, id + "F18", {"operationType" : BooleanOperationType.INTERSECTION, "tools" : qUnion([Q0, Q1])});
        }
    });
